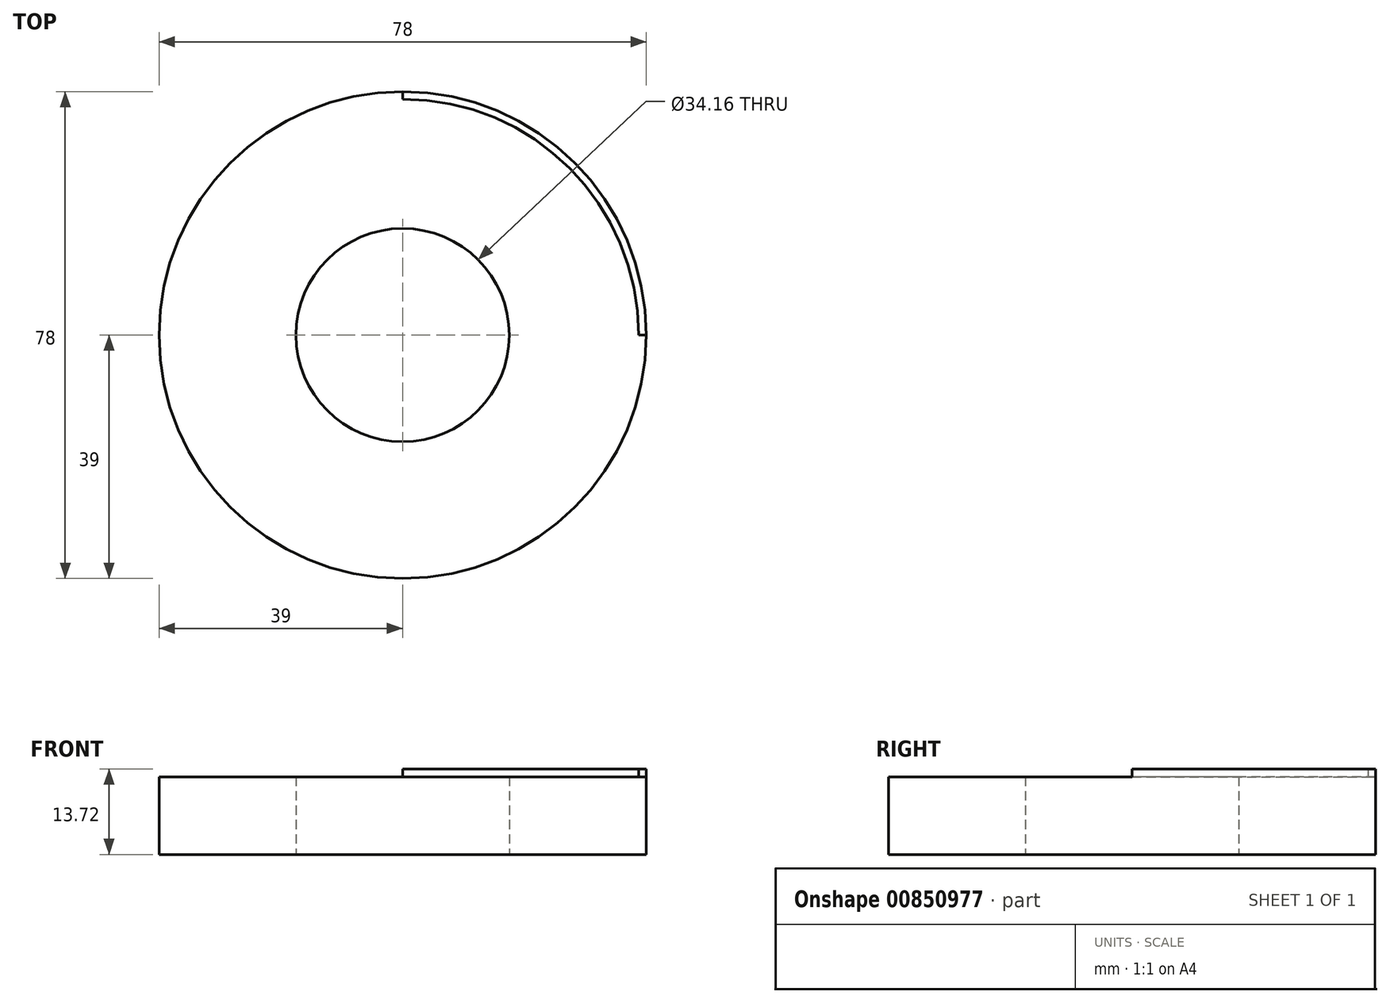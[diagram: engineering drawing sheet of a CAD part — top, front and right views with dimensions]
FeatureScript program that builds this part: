
annotation { "Feature Type Name" : "Feature", "Feature Type Description" : "" }
export const myFeature = defineFeature(function(context is Context, id is Id, definition is map)
    precondition{}
    {
        {
            var Q0;
            Q0=qCreatedBy(makeId("Top.planeOp"),FACE);
            var sketch = newSketch(context, id + "F0", { "sketchPlane" : qUnion([Q0])});
            skCircle(sketch, "E0", {"center": v(0, 0) * mm, "radius": 39 * mm});
            skCircle(sketch, "E1", {"center": v(0, 0) * mm, "radius": 17.08 * mm});
            skSolve(sketch);
        }
        {
            var Q0;
            Q0=makeQuery(id+"F0.imprint","IMPRINT",FACE,{"disambiguationData":[TD([[makeQuery(id+"F0.imprint","IMPRINT",EDGE,{"derivedFrom":sQuery(id+"F0.wireOp",EDGE,"E0")}),1.0]])]});
            extrude(context, id + "F1", {"entities" : qUnion([Q0]), "depth" : 12.45 * mm, "offsetDistance" : 25.4 * mm});
        }
        {
            var Q0;
            Q0=makeQuery(id+"F1.opExtrude","CAP_FACE",FACE,{"disambiguationData":[OSD([sQuery(id+"F0.wireOp",EDGE,"E0"),sQuery(id+"F0.wireOp",EDGE,"E1")])],"isStart":false});
            var sketch = newSketch(context, id + "F2", { "sketchPlane" : qUnion([Q0])});
            skCircle(sketch, "E2", {"center": v(0, 0) * mm, "radius": 21.54 * mm});
            skCircle(sketch, "E3", {"center": v(0, 0) * mm, "radius": 22.25 * mm});
            skSolve(sketch);
        }
        {
            var Q0;
            Q0=makeQuery(id+"F1.opExtrude","CAP_FACE",FACE,{"disambiguationData":[OSD([sQuery(id+"F0.wireOp",EDGE,"E0"),sQuery(id+"F0.wireOp",EDGE,"E1")])],"isStart":false});
            var sketch = newSketch(context, id + "F3", { "sketchPlane" : qUnion([Q0])});
            skArc(sketch, "E4", {"start": v(37.81, 0) * mm, "mid": v(26.74, 26.74) * mm, "end": v(0, 37.81) * mm});
            skLineSegment(sketch, "E5", {"start": v(-39, 0) * mm, "end": v(-37.81, 0) * mm});
            skLineSegment(sketch, "E6.trimOffspring", {"start": v(37.81, 0) * mm, "end": v(39, 0) * mm});
            skLineSegment(sketch, "E7", {"start": v(0, 37.81) * mm, "end": v(0, 39) * mm});
            skSolve(sketch);
        }
        {
            var Q0;
            Q0=makeQuery(id+"F3.imprint","IMPRINT",FACE,{"disambiguationData":[TD([[makeQuery(id+"F3.imprint","IMPRINT",EDGE,{"derivedFrom":sQuery(id+"F3.wireOp",EDGE,"E4")}),-1.0]])]});
            extrude(context, id + "F4", {"entities" : qUnion([Q0]), "operationType" : NewBodyOperationType.ADD, "depth" : 1.27 * mm, "offsetDistance" : 25.4 * mm});
        }
    });
